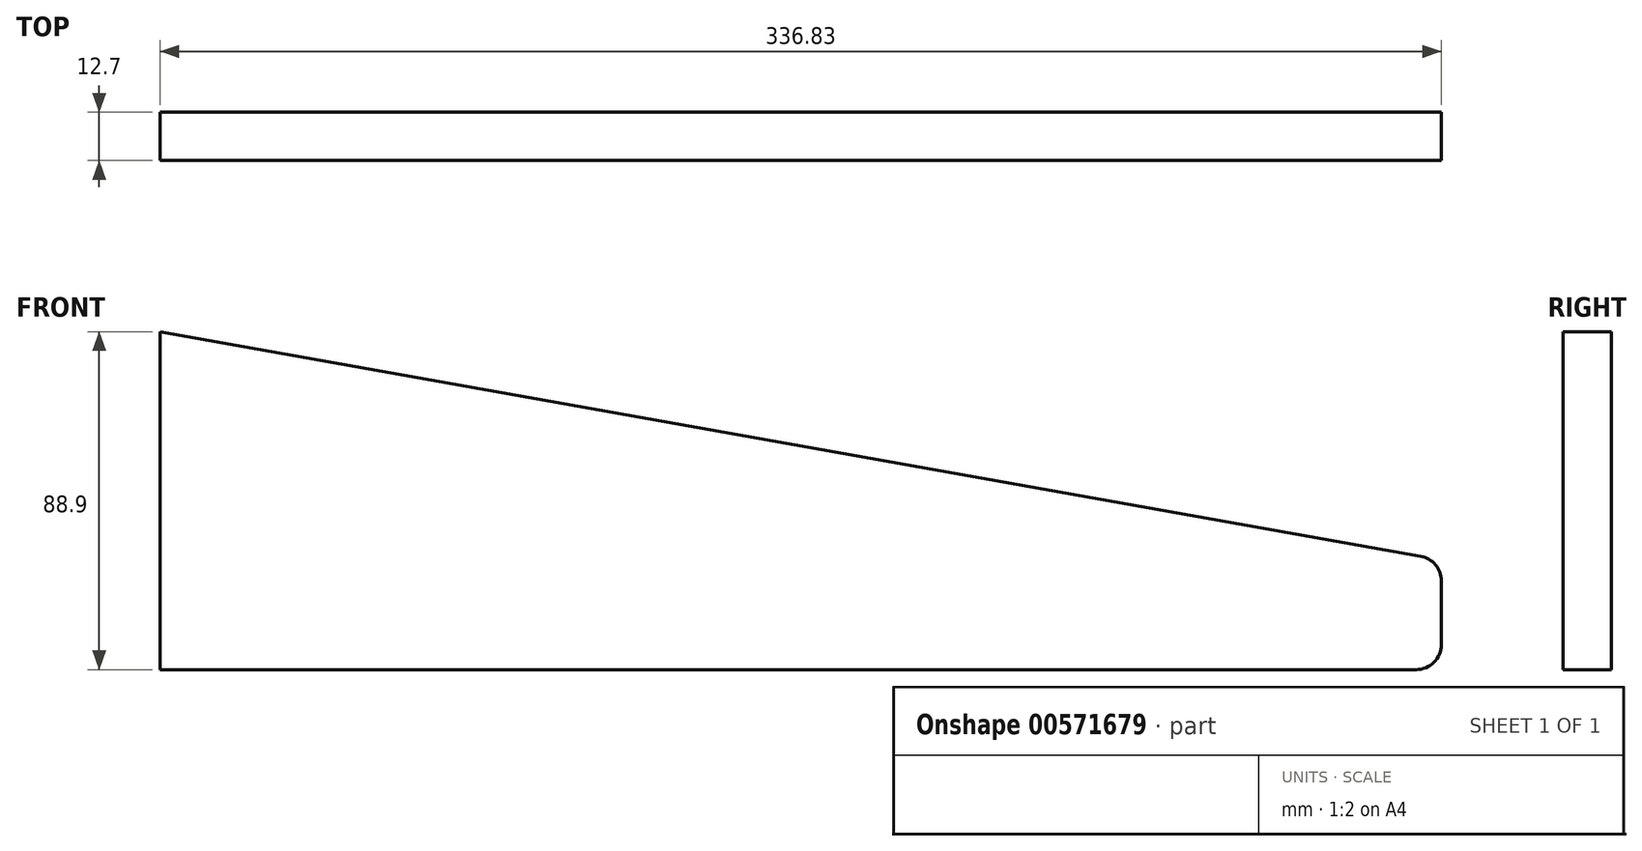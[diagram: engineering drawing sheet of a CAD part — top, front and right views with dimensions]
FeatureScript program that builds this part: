
annotation { "Feature Type Name" : "Feature", "Feature Type Description" : "" }
export const myFeature = defineFeature(function(context is Context, id is Id, definition is map)
    precondition{}
    {
        {
            var Q0;
            Q0=qCreatedBy(makeId("Front.planeOp"),FACE);
            var sketch = newSketch(context, id + "F0", { "sketchPlane" : qUnion([Q0])});
            skLineSegment(sketch, "E0", {"start": v(-178.9, 44) * mm, "end": v(-178.9, -44.9) * mm});
            skLineSegment(sketch, "E1", {"start": v(-178.9, -44.9) * mm, "end": v(151.3, -44.9) * mm});
            skLineSegment(sketch, "E2", {"start": v(157.92, -38.26) * mm, "end": v(157.92, -21.58) * mm});
            skLineSegment(sketch, "E3", {"start": v(152.46, -15.05) * mm, "end": v(-178.9, 44) * mm});
            skPoint(sketch, "E4.visualSharp", {"position": v(157.92, -16.03) * mm});
            skArc(sketch, "E4.filletArc", {"start": v(157.92, -21.58) * mm, "mid": v(156.38, -17.32) * mm, "end": v(152.46, -15.05) * mm});
            skPoint(sketch, "E5.visualSharp", {"position": v(157.92, -44.9) * mm});
            skArc(sketch, "E5.filletArc", {"start": v(151.3, -44.9) * mm, "mid": v(155.98, -42.95) * mm, "end": v(157.92, -38.26) * mm});
            skSolve(sketch);
        }
        {
            var Q0;
            Q0 = qSketchRegion(id + "F0", true);
            extrude(context, id + "F1", {"entities" : qUnion([Q0]), "depth" : 12.7 * mm, "offsetDistance" : 25.4 * mm});
        }
    });
